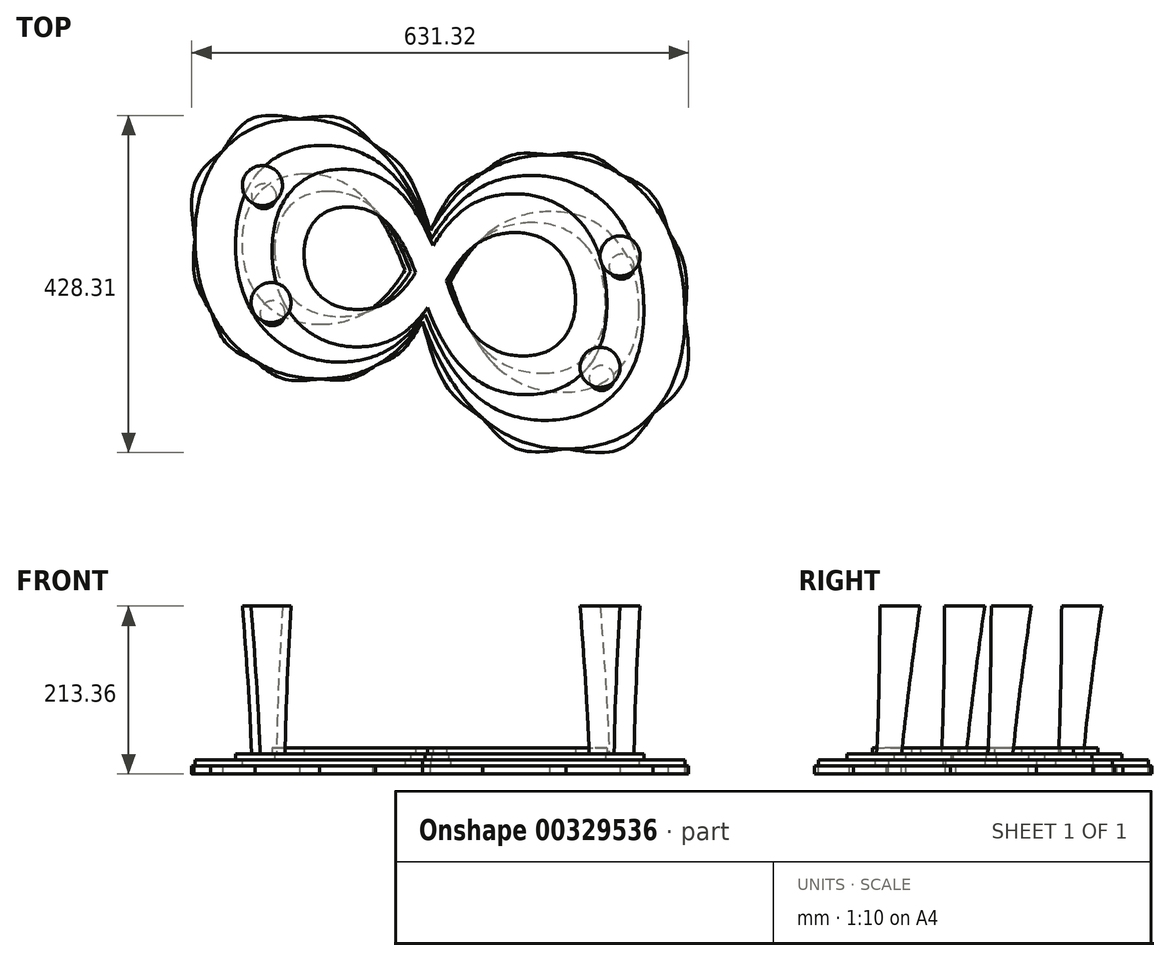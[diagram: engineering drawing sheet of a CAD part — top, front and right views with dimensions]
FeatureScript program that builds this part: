
annotation { "Feature Type Name" : "Feature", "Feature Type Description" : "" }
export const myFeature = defineFeature(function(context is Context, id is Id, definition is map)
    precondition{}
    {
        {
            var Q0;
            Q0=qCreatedBy(makeId("Top.planeOp"),FACE);
            var sketch = newSketch(context, id + "F0", { "sketchPlane" : qUnion([Q0])});
            skText(sketch, "E0", { "text": "8", "fontName": "OpenSans-Italic.ttf"});
            const initialGuessF0  = {"E0": [0.3048, -0.25691, 0, 1, 0.6096]};
            skSetInitialGuess(sketch, initialGuessF0);
            skSolve(sketch);
        }
        {
            var Q0;
            Q0=makeQuery(id+"F0.imprint","IMPRINT",FACE,{"disambiguationData":[TD([[makeQuery(id+"F0.imprint","IMPRINT",EDGE,{"derivedFrom":sQuery(id+"F0.wireOp",EDGE,"E0.sketch_text.stroke-0")}),-1.0]])]});
            extrude(context, id + "F1", {"entities" : qUnion([Q0]), "depth" : 7.62 * mm});
        }
        {
            var Q0;
            Q0=makeQuery(id+"F1.opExtrude","CAP_FACE",FACE,{"disambiguationData":[OSD([sQuery(id+"F0.wireOp",EDGE,"E0.sketch_text.stroke-0"),sQuery(id+"F0.wireOp",EDGE,"E0.sketch_text.stroke-1"),sQuery(id+"F0.wireOp",EDGE,"E0.sketch_text.stroke-2"),sQuery(id+"F0.wireOp",EDGE,"E0.sketch_text.stroke-3"),sQuery(id+"F0.wireOp",EDGE,"E0.sketch_text.stroke-4"),sQuery(id+"F0.wireOp",EDGE,"E0.sketch_text.stroke-5"),sQuery(id+"F0.wireOp",EDGE,"E0.sketch_text.stroke-6"),sQuery(id+"F0.wireOp",EDGE,"E0.sketch_text.stroke-7"),sQuery(id+"F0.wireOp",EDGE,"E0.sketch_text.stroke-8"),sQuery(id+"F0.wireOp",EDGE,"E0.sketch_text.stroke-9"),sQuery(id+"F0.wireOp",EDGE,"E0.sketch_text.stroke-10"),sQuery(id+"F0.wireOp",EDGE,"E0.sketch_text.stroke-11"),sQuery(id+"F0.wireOp",EDGE,"E0.sketch_text.stroke-12"),sQuery(id+"F0.wireOp",EDGE,"E0.sketch_text.stroke-13"),sQuery(id+"F0.wireOp",EDGE,"E0.sketch_text.stroke-14"),sQuery(id+"F0.wireOp",EDGE,"E0.sketch_text.stroke-15"),sQuery(id+"F0.wireOp",EDGE,"E0.sketch_text.stroke-16"),sQuery(id+"F0.wireOp",EDGE,"E0.sketch_text.stroke-17"),sQuery(id+"F0.wireOp",EDGE,"E0.sketch_text.stroke-18"),sQuery(id+"F0.wireOp",EDGE,"E0.sketch_text.stroke-19"),sQuery(id+"F0.wireOp",EDGE,"E0.sketch_text.stroke-20"),sQuery(id+"F0.wireOp",EDGE,"E0.sketch_text.stroke-21"),sQuery(id+"F0.wireOp",EDGE,"E0.sketch_text.stroke-22"),sQuery(id+"F0.wireOp",EDGE,"E0.sketch_text.stroke-23"),sQuery(id+"F0.wireOp",EDGE,"E0.sketch_text.stroke-24"),sQuery(id+"F0.wireOp",EDGE,"E0.sketch_text.stroke-25"),sQuery(id+"F0.wireOp",EDGE,"E0.sketch_text.stroke-26"),sQuery(id+"F0.wireOp",EDGE,"E0.sketch_text.stroke-27"),sQuery(id+"F0.wireOp",EDGE,"E0.sketch_text.stroke-28"),sQuery(id+"F0.wireOp",EDGE,"E0.sketch_text.stroke-29"),sQuery(id+"F0.wireOp",EDGE,"E0.sketch_text.stroke-30"),sQuery(id+"F0.wireOp",EDGE,"E0.sketch_text.stroke-31"),sQuery(id+"F0.wireOp",EDGE,"E0.sketch_text.stroke-32"),sQuery(id+"F0.wireOp",EDGE,"E0.sketch_text.stroke-33")])],"isStart":false});
            var sketch = newSketch(context, id + "F2", { "sketchPlane" : qUnion([Q0])});
            skText(sketch, "E1", { "text": "8", "fontName": "OpenSans-Italic.ttf"});
            const initialGuessF2  = {"E1": [0.254, -0.2141, 0, 1, 0.508]};
            skSetInitialGuess(sketch, initialGuessF2);
            skSolve(sketch);
        }
        {
            var Q0;
            Q0 = qSketchRegion(id + "F2", true);
            extrude(context, id + "F3", {"entities" : qUnion([Q0]), "operationType" : NewBodyOperationType.ADD, "depth" : 7.62 * mm});
        }
        {
            var Q0;
            Q0=makeQuery(id+"F3.opExtrude","CAP_FACE",FACE,{"disambiguationData":[OSD([sQuery(id+"F2.wireOp",EDGE,"E1.sketch_text.stroke-0"),sQuery(id+"F2.wireOp",EDGE,"E1.sketch_text.stroke-1"),sQuery(id+"F2.wireOp",EDGE,"E1.sketch_text.stroke-2"),sQuery(id+"F2.wireOp",EDGE,"E1.sketch_text.stroke-3"),sQuery(id+"F2.wireOp",EDGE,"E1.sketch_text.stroke-4"),sQuery(id+"F2.wireOp",EDGE,"E1.sketch_text.stroke-5"),sQuery(id+"F2.wireOp",EDGE,"E1.sketch_text.stroke-6"),sQuery(id+"F2.wireOp",EDGE,"E1.sketch_text.stroke-7"),sQuery(id+"F2.wireOp",EDGE,"E1.sketch_text.stroke-8"),sQuery(id+"F2.wireOp",EDGE,"E1.sketch_text.stroke-9"),sQuery(id+"F2.wireOp",EDGE,"E1.sketch_text.stroke-10"),sQuery(id+"F2.wireOp",EDGE,"E1.sketch_text.stroke-11"),sQuery(id+"F2.wireOp",EDGE,"E1.sketch_text.stroke-12"),sQuery(id+"F2.wireOp",EDGE,"E1.sketch_text.stroke-13"),sQuery(id+"F2.wireOp",EDGE,"E1.sketch_text.stroke-14"),sQuery(id+"F2.wireOp",EDGE,"E1.sketch_text.stroke-15"),sQuery(id+"F2.wireOp",EDGE,"E1.sketch_text.stroke-16"),sQuery(id+"F2.wireOp",EDGE,"E1.sketch_text.stroke-17"),sQuery(id+"F2.wireOp",EDGE,"E1.sketch_text.stroke-18"),sQuery(id+"F2.wireOp",EDGE,"E1.sketch_text.stroke-19"),sQuery(id+"F2.wireOp",EDGE,"E1.sketch_text.stroke-20"),sQuery(id+"F2.wireOp",EDGE,"E1.sketch_text.stroke-21"),sQuery(id+"F2.wireOp",EDGE,"E1.sketch_text.stroke-22"),sQuery(id+"F2.wireOp",EDGE,"E1.sketch_text.stroke-23"),sQuery(id+"F2.wireOp",EDGE,"E1.sketch_text.stroke-24"),sQuery(id+"F2.wireOp",EDGE,"E1.sketch_text.stroke-25"),sQuery(id+"F2.wireOp",EDGE,"E1.sketch_text.stroke-26"),sQuery(id+"F2.wireOp",EDGE,"E1.sketch_text.stroke-27"),sQuery(id+"F2.wireOp",EDGE,"E1.sketch_text.stroke-28"),sQuery(id+"F2.wireOp",EDGE,"E1.sketch_text.stroke-29"),sQuery(id+"F2.wireOp",EDGE,"E1.sketch_text.stroke-30"),sQuery(id+"F2.wireOp",EDGE,"E1.sketch_text.stroke-31"),sQuery(id+"F2.wireOp",EDGE,"E1.sketch_text.stroke-32"),sQuery(id+"F2.wireOp",EDGE,"E1.sketch_text.stroke-33")])],"isStart":false});
            var sketch = newSketch(context, id + "F4", { "sketchPlane" : qUnion([Q0])});
            skText(sketch, "E2", { "text": "8", "fontName": "OpenSans-Italic.ttf"});
            const initialGuessF4  = {"E2": [0.20828, -0.17556, 0, 1, 0.41656]};
            skSetInitialGuess(sketch, initialGuessF4);
            skSolve(sketch);
        }
        {
            var Q0;
            Q0 = qSketchRegion(id + "F4", true);
            extrude(context, id + "F5", {"entities" : qUnion([Q0]), "operationType" : NewBodyOperationType.ADD, "depth" : 7.62 * mm});
        }
        {
            var Q0;
            Q0=makeQuery(id+"F1.opExtrude","CAP_FACE",FACE,{"disambiguationData":[OSD([sQuery(id+"F0.wireOp",EDGE,"E0.sketch_text.stroke-0"),sQuery(id+"F0.wireOp",EDGE,"E0.sketch_text.stroke-1"),sQuery(id+"F0.wireOp",EDGE,"E0.sketch_text.stroke-2"),sQuery(id+"F0.wireOp",EDGE,"E0.sketch_text.stroke-3"),sQuery(id+"F0.wireOp",EDGE,"E0.sketch_text.stroke-4"),sQuery(id+"F0.wireOp",EDGE,"E0.sketch_text.stroke-5"),sQuery(id+"F0.wireOp",EDGE,"E0.sketch_text.stroke-6"),sQuery(id+"F0.wireOp",EDGE,"E0.sketch_text.stroke-7"),sQuery(id+"F0.wireOp",EDGE,"E0.sketch_text.stroke-8"),sQuery(id+"F0.wireOp",EDGE,"E0.sketch_text.stroke-9"),sQuery(id+"F0.wireOp",EDGE,"E0.sketch_text.stroke-10"),sQuery(id+"F0.wireOp",EDGE,"E0.sketch_text.stroke-11"),sQuery(id+"F0.wireOp",EDGE,"E0.sketch_text.stroke-12"),sQuery(id+"F0.wireOp",EDGE,"E0.sketch_text.stroke-13"),sQuery(id+"F0.wireOp",EDGE,"E0.sketch_text.stroke-14"),sQuery(id+"F0.wireOp",EDGE,"E0.sketch_text.stroke-15"),sQuery(id+"F0.wireOp",EDGE,"E0.sketch_text.stroke-16"),sQuery(id+"F0.wireOp",EDGE,"E0.sketch_text.stroke-17"),sQuery(id+"F0.wireOp",EDGE,"E0.sketch_text.stroke-18"),sQuery(id+"F0.wireOp",EDGE,"E0.sketch_text.stroke-19"),sQuery(id+"F0.wireOp",EDGE,"E0.sketch_text.stroke-20"),sQuery(id+"F0.wireOp",EDGE,"E0.sketch_text.stroke-21"),sQuery(id+"F0.wireOp",EDGE,"E0.sketch_text.stroke-22"),sQuery(id+"F0.wireOp",EDGE,"E0.sketch_text.stroke-23"),sQuery(id+"F0.wireOp",EDGE,"E0.sketch_text.stroke-24"),sQuery(id+"F0.wireOp",EDGE,"E0.sketch_text.stroke-25"),sQuery(id+"F0.wireOp",EDGE,"E0.sketch_text.stroke-26"),sQuery(id+"F0.wireOp",EDGE,"E0.sketch_text.stroke-27"),sQuery(id+"F0.wireOp",EDGE,"E0.sketch_text.stroke-28"),sQuery(id+"F0.wireOp",EDGE,"E0.sketch_text.stroke-29"),sQuery(id+"F0.wireOp",EDGE,"E0.sketch_text.stroke-30"),sQuery(id+"F0.wireOp",EDGE,"E0.sketch_text.stroke-31"),sQuery(id+"F0.wireOp",EDGE,"E0.sketch_text.stroke-32"),sQuery(id+"F0.wireOp",EDGE,"E0.sketch_text.stroke-33")])],"isStart":true});
            var sketch = newSketch(context, id + "F6", { "sketchPlane" : qUnion([Q0])});
            skFitSpline(sketch, "E3.0", {"points": [v(231.44, -131.3) * mm, v(270.93, -106.5) * mm, v(292.03, -60) * mm]});
            skFitSpline(sketch, "E4.0", {"points": [v(141.55, -156.1) * mm, v(191.96, -156.1) * mm, v(231.44, -131.3) * mm]});
            skFitSpline(sketch, "E5.0", {"points": [v(57.94, -134.2) * mm, v(93.93, -156.1) * mm, v(141.55, -156.1) * mm]});
            skFitSpline(sketch, "E6.0", {"points": [v(-10.19, -59.8) * mm, v(21.96, -112.32) * mm, v(57.94, -134.2) * mm]});
            skFitSpline(sketch, "E7.0", {"points": [v(-82.95, -169.73) * mm, v(-43.26, -137.45) * mm, v(-10.19, -59.8) * mm]});
            skFitSpline(sketch, "E8.0", {"points": [v(-175.95, -202) * mm, v(-122.63, -202) * mm, v(-82.95, -169.73) * mm]});
            skFitSpline(sketch, "E9.0", {"points": [v(-273.38, -161.66) * mm, v(-237.6, -202) * mm, v(-175.95, -202) * mm]});
            skFitSpline(sketch, "E10.0", {"points": [v(-309.17, -49.48) * mm, v(-309.17, -121.31) * mm, v(-273.38, -161.66) * mm]});
            skFitSpline(sketch, "E11.0", {"points": [v(-289.12, 42.33) * mm, v(-309.17, 1.46) * mm, v(-309.17, -49.48) * mm]});
            skFitSpline(sketch, "E12.0", {"points": [v(-232.9, 105.77) * mm, v(-269.08, 83.21) * mm, v(-289.12, 42.33) * mm]});
            skFitSpline(sketch, "E13.0", {"points": [v(-150.81, 128.32) * mm, v(-196.72, 128.32) * mm, v(-232.9, 105.77) * mm]});
            skFitSpline(sketch, "E14.0", {"points": [v(-79.9, 111.59) * mm, v(-111.13, 128.32) * mm, v(-150.81, 128.32) * mm]});
            skFitSpline(sketch, "E15.0", {"points": [v(-20.1, 55.56) * mm, v(-48.68, 94.85) * mm, v(-79.9, 111.59) * mm]});
            skFitSpline(sketch, "E16.0", {"points": [v(55.9, 177.93) * mm, v(11.24, 138.64) * mm, v(-20.1, 55.56) * mm]});
            skFitSpline(sketch, "E17.0", {"points": [v(161.8, 217.22) * mm, v(100.54, 217.22) * mm, v(55.9, 177.93) * mm]});
            skFitSpline(sketch, "E18.0", {"points": [v(272.39, 172.57) * mm, v(231.64, 217.22) * mm, v(161.8, 217.22) * mm]});
            skFitSpline(sketch, "E19.0", {"points": [v(313.13, 49.34) * mm, v(313.13, 127.93) * mm, v(272.39, 172.57) * mm]});
            skFitSpline(sketch, "E20.0.0", {"points": [v(272.39, 172.57) * mm, v(313.13, 127.93) * mm, v(313.13, 49.34) * mm]});
            skFitSpline(sketch, "E20.0.2", {"points": [v(313.13, 49.34) * mm, v(313.13, 127.93) * mm, v(272.39, 172.57) * mm]});
            skFitSpline(sketch, "E21.0", {"points": [v(292.03, -60) * mm, v(313.13, -13.5) * mm, v(313.13, 49.34) * mm]});
            skSolve(sketch);
        }
        {
            var Q0;
            Q0 = qSketchRegion(id + "F6", true);
            extrude(context, id + "F7", {"entities" : qUnion([Q0]), "depth" : 10.16 * mm});
        }
        {
            var Q0;
            {var subQ0=sQuery(id+"F2.wireOp",EDGE,"E1.sketch_text.stroke-17");var subQ1=sQuery(id+"F2.wireOp",EDGE,"E1.sketch_text.stroke-9");var subQ2=sQuery(id+"F2.wireOp",EDGE,"E1.sketch_text.stroke-16");var subQ3=sQuery(id+"F2.wireOp",EDGE,"E1.sketch_text.stroke-8");var subQ4=sQuery(id+"F2.wireOp",EDGE,"E1.sketch_text.stroke-15");var subQ5=sQuery(id+"F2.wireOp",EDGE,"E1.sketch_text.stroke-7");var subQ6=sQuery(id+"F2.wireOp",EDGE,"E1.sketch_text.stroke-14");var subQ7=sQuery(id+"F2.wireOp",EDGE,"E1.sketch_text.stroke-13");var subQ8=sQuery(id+"F2.wireOp",EDGE,"E1.sketch_text.stroke-12");var subQ9=sQuery(id+"F2.wireOp",EDGE,"E1.sketch_text.stroke-4");var subQ10=sQuery(id+"F2.wireOp",EDGE,"E1.sketch_text.stroke-11");var subQ11=sQuery(id+"F2.wireOp",EDGE,"E1.sketch_text.stroke-10");var subQ12=sQuery(id+"F2.wireOp",EDGE,"E1.sketch_text.stroke-2");var subQ13=sQuery(id+"F2.wireOp",EDGE,"E1.sketch_text.stroke-1");var subQ14=sQuery(id+"F2.wireOp",EDGE,"E1.sketch_text.stroke-3");var subQ15=sQuery(id+"F2.wireOp",EDGE,"E1.sketch_text.stroke-0");var subQ16=sQuery(id+"F2.wireOp",EDGE,"E1.sketch_text.stroke-5");var subQ17=sQuery(id+"F2.wireOp",EDGE,"E1.sketch_text.stroke-6");Q0=makeQuery(id+"F5.boolean.opBoolean","SPLIT",FACE,{"disambiguationData":[TD([makeQuery(id+"F3.opExtrude","SWEPT_FACE",FACE,{"disambiguationData":[OSD([subQ15])]})])],"derivedFrom":makeQuery(id+"F3.opExtrude","CAP_FACE",FACE,{"disambiguationData":[OSD([subQ15,subQ13,subQ12,subQ14,subQ9,subQ16,subQ17,subQ5,subQ3,subQ1,subQ11,subQ10,subQ8,subQ7,subQ6,subQ4,subQ2,subQ0,sQuery(id+"F2.wireOp",EDGE,"E1.sketch_text.stroke-18"),sQuery(id+"F2.wireOp",EDGE,"E1.sketch_text.stroke-19"),sQuery(id+"F2.wireOp",EDGE,"E1.sketch_text.stroke-20"),sQuery(id+"F2.wireOp",EDGE,"E1.sketch_text.stroke-21"),sQuery(id+"F2.wireOp",EDGE,"E1.sketch_text.stroke-22"),sQuery(id+"F2.wireOp",EDGE,"E1.sketch_text.stroke-23"),sQuery(id+"F2.wireOp",EDGE,"E1.sketch_text.stroke-24"),sQuery(id+"F2.wireOp",EDGE,"E1.sketch_text.stroke-25"),sQuery(id+"F2.wireOp",EDGE,"E1.sketch_text.stroke-26"),sQuery(id+"F2.wireOp",EDGE,"E1.sketch_text.stroke-27"),sQuery(id+"F2.wireOp",EDGE,"E1.sketch_text.stroke-28"),sQuery(id+"F2.wireOp",EDGE,"E1.sketch_text.stroke-29"),sQuery(id+"F2.wireOp",EDGE,"E1.sketch_text.stroke-30"),sQuery(id+"F2.wireOp",EDGE,"E1.sketch_text.stroke-31"),sQuery(id+"F2.wireOp",EDGE,"E1.sketch_text.stroke-32"),sQuery(id+"F2.wireOp",EDGE,"E1.sketch_text.stroke-33")])],"isStart":false})});}
            var sketch = newSketch(context, id + "F8", { "sketchPlane" : qUnion([Q0])});
            skCircle(sketch, "E22", {"center": v(-210.6, -44.99) * mm, "radius": 15.88 * mm});
            skCircle(sketch, "E23", {"center": v(-221.5, 103.62) * mm, "radius": 15.88 * mm});
            skCircle(sketch, "E24", {"center": v(207.38, -127.3) * mm, "radius": 15.88 * mm});
            skCircle(sketch, "E25", {"center": v(232.76, 14.15) * mm, "radius": 15.88 * mm});
            skLineSegment(sketch, "E26", {"start": v(-210.6, -44.99) * mm, "end": v(207.38, -127.3) * mm, "construction": true});
            skLineSegment(sketch, "E27", {"start": v(-221.5, 103.62) * mm, "end": v(232.76, 14.15) * mm, "construction": true});
            skSolve(sketch);
        }
        {
            var Q0;
            Q0=qCreatedBy(makeId("Top.planeOp"),FACE);
            cPlane(context, id + "F9", {"entities" : qUnion([Q0]), "cplaneType" : CPlaneType.OFFSET, "offset" : 203.2 * mm, "width" : 152.4 * mm, "height" : 152.4 * mm});
        }
        {
            var Q0;
            Q0=qCreatedBy(id+"F9.planeOp",FACE);
            var sketch = newSketch(context, id + "F10", { "sketchPlane" : qUnion([Q0])});
            skCircle(sketch, "E28", {"center": v(-212.6, -31.36) * mm, "radius": 15.88 * mm, "construction": true});
            skCircle(sketch, "E29", {"center": v(-223.51, 117.25) * mm, "radius": 15.88 * mm, "construction": true});
            skCircle(sketch, "E30", {"center": v(205.37, -113.68) * mm, "radius": 15.88 * mm, "construction": true});
            skCircle(sketch, "E31", {"center": v(230.75, 27.78) * mm, "radius": 15.88 * mm, "construction": true});
            skLineSegment(sketch, "E32", {"start": v(-212.6, -31.36) * mm, "end": v(205.37, -113.68) * mm, "construction": true});
            skLineSegment(sketch, "E33", {"start": v(-223.51, 117.25) * mm, "end": v(230.75, 27.78) * mm, "construction": true});
            skCircle(sketch, "E34", {"center": v(230.75, 27.78) * mm, "radius": 25.4 * mm});
            skCircle(sketch, "E35", {"center": v(205.37, -113.68) * mm, "radius": 25.4 * mm});
            skCircle(sketch, "E36", {"center": v(-223.51, 117.25) * mm, "radius": 25.4 * mm});
            skCircle(sketch, "E37", {"center": v(-212.6, -31.36) * mm, "radius": 25.4 * mm});
            skSolve(sketch);
        }
        {
            var Q1;
            Q1=makeQuery(id+"F8.imprint","IMPRINT",FACE,{"disambiguationData":[TD([[makeQuery(id+"F8.imprint","IMPRINT",EDGE,{"derivedFrom":sQuery(id+"F8.wireOp",EDGE,"E24")}),1.0]])]});
            var Q2;
            Q2=makeQuery(id+"F10.imprint","IMPRINT",FACE,{"disambiguationData":[TD([[makeQuery(id+"F10.imprint","IMPRINT",EDGE,{"derivedFrom":sQuery(id+"F10.wireOp",EDGE,"E35")}),1.0]])]});
            loft(context, id + "F11", {"sheetProfilesArray" : [{ "sheetProfileEntities" : qUnion([Q1]) }, { "sheetProfileEntities" : qUnion([Q2]) }]});
        }
        {
            var Q1;
            Q1=makeQuery(id+"F8.imprint","IMPRINT",FACE,{"disambiguationData":[TD([[makeQuery(id+"F8.imprint","IMPRINT",EDGE,{"derivedFrom":sQuery(id+"F8.wireOp",EDGE,"E25")}),1.0]])]});
            var Q2;
            Q2=makeQuery(id+"F10.imprint","IMPRINT",FACE,{"disambiguationData":[TD([[makeQuery(id+"F10.imprint","IMPRINT",EDGE,{"derivedFrom":sQuery(id+"F10.wireOp",EDGE,"E34")}),1.0]])]});
            loft(context, id + "F12", {"sheetProfilesArray" : [{ "sheetProfileEntities" : qUnion([Q1]) }, { "sheetProfileEntities" : qUnion([Q2]) }]});
        }
        {
            var Q1;
            Q1=makeQuery(id+"F8.imprint","IMPRINT",FACE,{"disambiguationData":[TD([[makeQuery(id+"F8.imprint","IMPRINT",EDGE,{"derivedFrom":sQuery(id+"F8.wireOp",EDGE,"E23")}),1.0]])]});
            var Q2;
            Q2=makeQuery(id+"F10.imprint","IMPRINT",FACE,{"disambiguationData":[TD([[makeQuery(id+"F10.imprint","IMPRINT",EDGE,{"derivedFrom":sQuery(id+"F10.wireOp",EDGE,"E36")}),1.0]])]});
            loft(context, id + "F13", {"sheetProfilesArray" : [{ "sheetProfileEntities" : qUnion([Q1]) }, { "sheetProfileEntities" : qUnion([Q2]) }]});
        }
        {
            var Q1;
            Q1=makeQuery(id+"F8.imprint","IMPRINT",FACE,{"disambiguationData":[TD([[makeQuery(id+"F8.imprint","IMPRINT",EDGE,{"derivedFrom":sQuery(id+"F8.wireOp",EDGE,"E22")}),1.0]])]});
            var Q2;
            Q2=makeQuery(id+"F10.imprint","IMPRINT",FACE,{"disambiguationData":[TD([[makeQuery(id+"F10.imprint","IMPRINT",EDGE,{"derivedFrom":sQuery(id+"F10.wireOp",EDGE,"E37")}),1.0]])]});
            loft(context, id + "F14", {"sheetProfilesArray" : [{ "sheetProfileEntities" : qUnion([Q1]) }, { "sheetProfileEntities" : qUnion([Q2]) }]});
        }
    });
